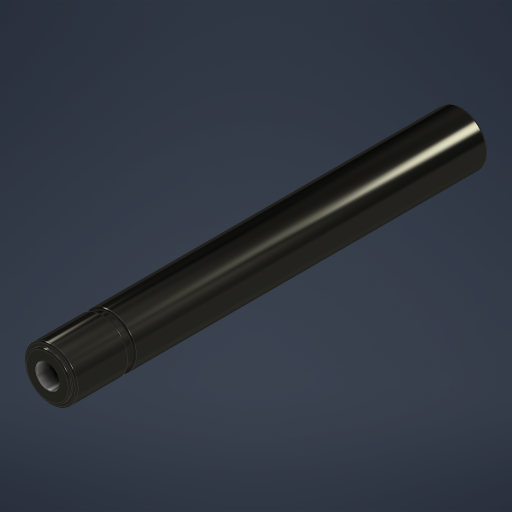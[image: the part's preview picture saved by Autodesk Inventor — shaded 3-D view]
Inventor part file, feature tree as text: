
AUTODESK INVENTOR PART (.ipt)
format: ipt  version: 2024 (Build 280153000, 153)  size: 238,080 bytes
history: native  units: in
note: dims shown in document units (in); Inventor stores cm internally (conversion verified against a paired STEP export)
features: fillet x1
ambient origin geometry x8: Origin, YZ Plane, XZ Plane, XY Plane, X Axis, Y Axis, Z Axis, Center Point
bodies: Solid1 (feature_tree)
feature tree (1):
  fillet  "Fillet1"  [1 undecoded]
note: 1 required parameter value undecoded (feature->parameter linkage not recoverable at this tier; creation-order binding heuristic only, values carry confidence <= 0.55)
